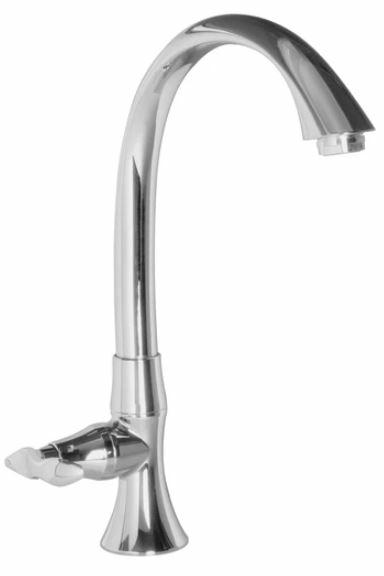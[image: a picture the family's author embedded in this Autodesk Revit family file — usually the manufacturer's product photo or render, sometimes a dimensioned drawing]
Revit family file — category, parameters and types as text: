
# Revit family: 01-1850-11 LLAVE MOVIL MESA TEDESCA
name_source: partatom
category: Plumbing Fixtures
revit_build: Autodesk Revit 2018 (Build: 20170223_1515(x64)
units: mm (PartAtom-declared; Revit-internal decimal feet)

## family parameters
Cut with Voids When Loaded = No
Host = Face
OmniClass Number = 23.31.11.00
Part Type = Normal
Room Calculation Point = No
Round Connector Dimension = Use Diameter
Shared = No

## types (1)
- 01-1850-11
    Alto Aireador = 240 mm  [stored 0.787402 ft]
    Alto brazo = 302 mm  [stored 0.990814 ft]
    Ancho a manija = 83 mm  [stored 0.27231 ft]
    Ancho brazo = 185 mm
    Base = 50 mm
    CW Connection = Yes
    Default Elevation = 0 mm  [stored 0 ft]
    Description = Monomando
    HW Connection = Yes
    Link Ficha Tecnica = http://infotecnica.gricol.com
    Manufacturer = Gricol
    Model = 01-1850-11
    Plástico - ABS Cromado = Plastico ABS Cromado
    Product Name = LLAVE MOVIL MESA TEDESCA
    Type Image = LLAVE MOVIL MESA TEDESCA.JPG
    URL = https://www.gricol.com
    Vent Connection = No
    Waste Connection = No

note: [stored X ft] marks values corroborated as IEEE doubles in the binary element streams (Revit-internal decimal feet)

## geometry (parser evidence)
native form markers: Blend x2, Sweep x4
no freeform markers — native parametric forms only
